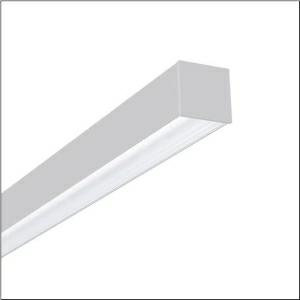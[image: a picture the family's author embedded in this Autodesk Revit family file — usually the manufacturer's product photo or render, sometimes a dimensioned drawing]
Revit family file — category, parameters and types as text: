
# Revit family: silica_r_5mx21dd1w4a_969a
name_source: partatom
category: Lighting Fixtures
units: mm (PartAtom-declared; Revit-internal decimal feet)

## family parameters
Cut with Voids When Loaded = No
Host = Face
Light Source = No
Part Type = Normal
Room Calculation Point = No
Round Connector Dimension = Use Diameter
Shared = No

## types (1)
- --- (1 x LED, 3140 lm, 22.6 W, 4000K)
    Apparent Load = 23 VA
    CIE Flux Codes = 47 79 96 100 100
    Color Rendering = 80
    Color Temperature = 4000K
    Default Elevation = 1800 mm
    Description = Silica®, office luminaire, of aluminium, opal, light emission: direct distribution, primary light characteristic: symmetric, installation type: surface-mounted, LED rated luminous flux: 3.010 lm, light colour: 840, colour temperature: 4000K, control gear: ECG DALI, with terminal, 3+2-pole, max. 2.5mm², mains connection: 230V, AC, 50/60Hz, rated input power: 24W, luminaire housing, of aluminium, traffic white (RAL 9016), length: 1.440 mm, width: 64 mm, height: 64mm, protection rating (complete): IP20, insulation class (complete): insulation class I (protective earthing), certification: CE, permissible ambient temperature for indoor applications: 0..+35°C, standard: EN 50419, packaging unit: 1 piece
    Height = 64 mm
    Lamp = 1 x LED
    Lamp Light Flux = 3140 lm
    Lamp Power = 22.6 W
    Lamp count = 1
    Length = 1442 mm
    Luminous efficacy = 139 lm/W
    Manufacturer = Siteco
    ModVariant = No
    Model = 5MX21DD1W4A
    Mounting Place = Ceiling
    Mounting Type = Surface mounted
    Number of Poles = 1
    OnlyDefault = Yes
    Power Factor = 1
    Product Name = Silica®
    Product group = office luminaire | ceiling mounted
    ProductGroupID = 302
    Protection Class = Protection class I
    Protection Degree = IP 20
    RLX_Detail_Level = 1
    RlxData = <blob elided: 22697 chars, md5=6804f5c2>
    Socket = socket
    Standby Power = 0 W
    System Light Flux = 3140 lm
    System Power = 23 W
    Type Comments = factory setting: luminous flux: 100 % | dim-lin: 254 | 125 mA
    Type Image = l_248206.jpg
    URL = http://relux.com
    VarID = @adj_128395
    Voltage = 0 V
    Weight = 0.00 kg
    Width = 65 mm

## geometry (parser evidence)
native form markers: Blend x4, Sweep x11
no freeform markers — native parametric forms only
